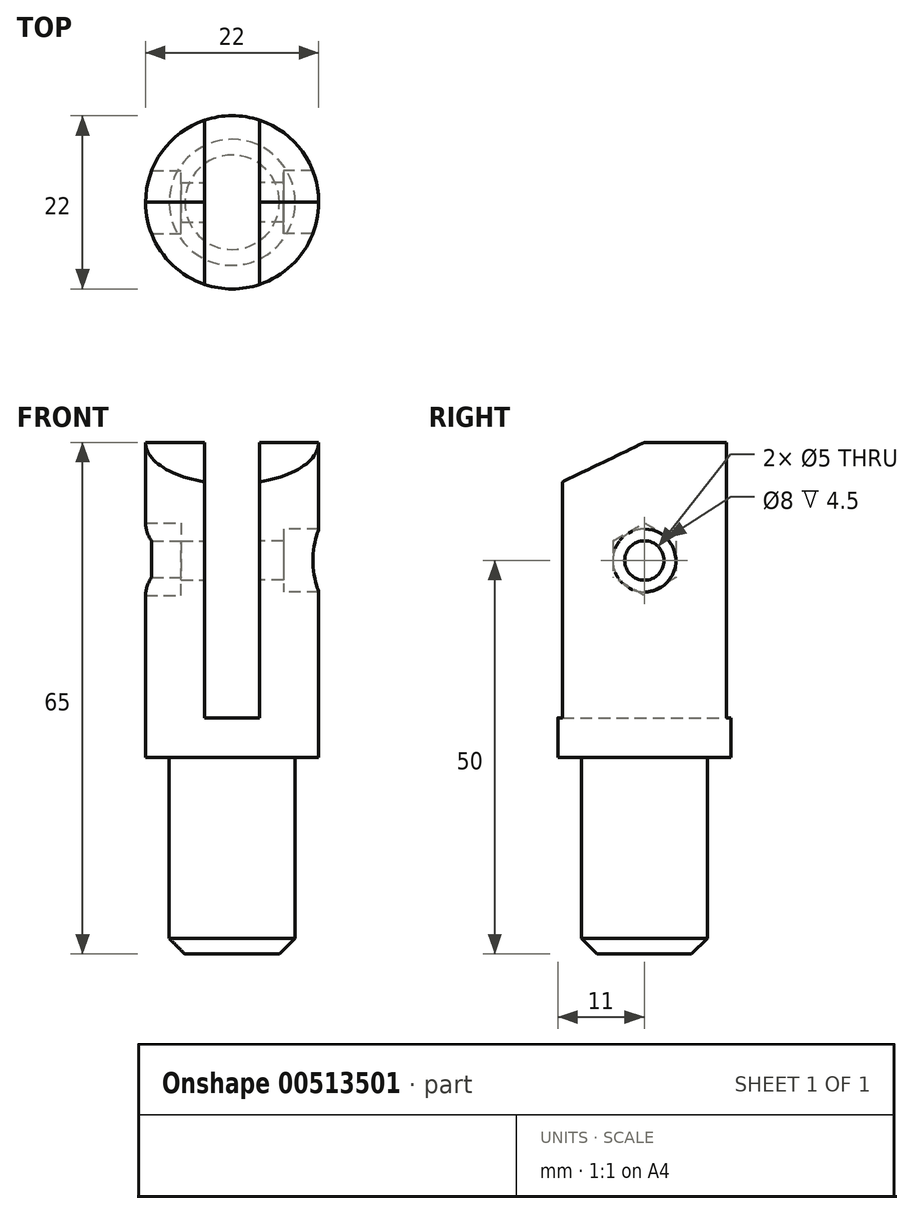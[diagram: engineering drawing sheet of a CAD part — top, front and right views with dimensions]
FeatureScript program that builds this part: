
annotation { "Feature Type Name" : "Feature", "Feature Type Description" : "" }
export const myFeature = defineFeature(function(context is Context, id is Id, definition is map)
    precondition{}
    {
        {
            var Q0;
            Q0=qCreatedBy(makeId("Top.planeOp"),FACE);
            var sketch = newSketch(context, id + "F0", { "sketchPlane" : qUnion([Q0])});
            skCircle(sketch, "E0", {"center": v(0, 0) * mm, "radius": 11 * mm});
            skSolve(sketch);
        }
        {
            var Q0;
            Q0=makeQuery(id+"F0.imprint","IMPRINT",FACE,{"disambiguationData":[TD([[makeQuery(id+"F0.imprint","IMPRINT",EDGE,{"derivedFrom":sQuery(id+"F0.wireOp",EDGE,"E0")}),1.0]])]});
            extrude(context, id + "F1", {"entities" : qUnion([Q0]), "depth" : 40 * mm, "offsetDistance" : 25 * mm});
        }
        {
            var Q0;
            Q0=makeQuery(id+"F1.opExtrude","CAP_FACE",FACE,{"disambiguationData":[OSD([sQuery(id+"F0.wireOp",EDGE,"E0")])],"isStart":false});
            var sketch = newSketch(context, id + "F2", { "sketchPlane" : qUnion([Q0])});
            skLineSegment(sketch, "E1.bottom", {"start": v(3.5, -20) * mm, "end": v(-3.5, -20) * mm});
            skLineSegment(sketch, "E1.top", {"start": v(3.5, 20) * mm, "end": v(-3.5, 20) * mm});
            skLineSegment(sketch, "E1.left", {"start": v(3.5, -20) * mm, "end": v(3.5, 20) * mm});
            skLineSegment(sketch, "E1.right", {"start": v(-3.5, -20) * mm, "end": v(-3.5, 20) * mm});
            skPoint(sketch, "E1.middle", {"position": v(0, 0) * mm});
            skSolve(sketch);
        }
        {
            var Q0;
            {var subQ0=sQuery(id+"F2.wireOp",EDGE,"E1.left");var subQ1=makeQuery(id+"F1.opExtrude","CAP_EDGE",EDGE,{"disambiguationData":[OSD([sQuery(id+"F0.wireOp",EDGE,"E0")])],"isStart":false});var subQ2=makeQuery(id+"F2.imprint","INTERSECT",VERTEX,{"disambiguationData":[OD(0.0)],"derivedFrom":[subQ1,subQ0]});Q0=makeQuery(id+"F2.imprint","IMPRINT",FACE,{"disambiguationData":[TD([[makeQuery(id+"F2.imprint","IMPRINT",EDGE,{"disambiguationData":[TD([[subQ2,-1.0]])],"derivedFrom":subQ0}),1.0]])]});}
            extrude(context, id + "F3", {"entities" : qUnion([Q0]), "operationType" : NewBodyOperationType.REMOVE, "oppositeDirection" : true, "depth" : 35 * mm, "offsetDistance" : 25 * mm});
        }
        {
            var Q0;
            Q0=makeQuery(id+"F3.boolean.opBoolean","COPY",FACE,{"derivedFrom":makeQuery(id+"F3.opExtrude","SWEPT_FACE",FACE,{"disambiguationData":[OSD([sQuery(id+"F2.wireOp",EDGE,"E1.right")])]})});
            var sketch = newSketch(context, id + "F4", { "sketchPlane" : qUnion([Q0])});
            skLineSegment(sketch, "E2", {"start": v(0, 40) * mm, "end": v(-10.43, 35) * mm});
            skSolve(sketch);
        }
        {
            var Q0;
            Q0=makeQuery(id+"F1.opExtrude","CAP_FACE",FACE,{"disambiguationData":[OSD([sQuery(id+"F0.wireOp",EDGE,"E0")])],"isStart":true});
            var sketch = newSketch(context, id + "F5", { "sketchPlane" : qUnion([Q0])});
            skCircle(sketch, "E3", {"center": v(0, 0) * mm, "radius": 8 * mm});
            skSolve(sketch);
        }
        {
            var Q0;
            {var subQ0=sQuery(id+"F4.wireOp",EDGE,"E2");Q0=makeQuery(id+"F4.imprint","IMPRINT",FACE,{"disambiguationData":[TD([[makeQuery(id+"F4.imprint","IMPRINT",EDGE,{"derivedFrom":subQ0}),-1.0]])]});}
            extrude(context, id + "F6", {"entities" : qUnion([Q0]), "operationType" : NewBodyOperationType.REMOVE, "endBound" : BoundingType.THROUGH_ALL, "oppositeDirection" : true, "depth" : 25 * mm, "offsetDistance" : 25 * mm});
        }
        {
            var Q0;
            Q0=makeQuery(id+"F3.boolean.opBoolean","COPY",FACE,{"derivedFrom":makeQuery(id+"F3.opExtrude","SWEPT_FACE",FACE,{"disambiguationData":[OSD([sQuery(id+"F2.wireOp",EDGE,"E1.left")])]})});
            var sketch = newSketch(context, id + "F7", { "sketchPlane" : qUnion([Q0])});
            skLineSegment(sketch, "E4", {"start": v(0, 40) * mm, "end": v(10.43, 35) * mm});
            skSolve(sketch);
        }
        {
            var Q0;
            {var subQ0=sQuery(id+"F7.wireOp",EDGE,"E4");Q0=makeQuery(id+"F7.imprint","IMPRINT",FACE,{"disambiguationData":[TD([[makeQuery(id+"F7.imprint","IMPRINT",EDGE,{"derivedFrom":subQ0}),1.0]])]});}
            extrude(context, id + "F8", {"entities" : qUnion([Q0]), "operationType" : NewBodyOperationType.REMOVE, "endBound" : BoundingType.THROUGH_ALL, "oppositeDirection" : true, "depth" : 25 * mm, "offsetDistance" : 25 * mm});
        }
        {
            var Q0;
            Q0=makeQuery(id+"F5.imprint","IMPRINT",FACE,{"disambiguationData":[TD([[makeQuery(id+"F5.imprint","IMPRINT",EDGE,{"derivedFrom":sQuery(id+"F5.wireOp",EDGE,"E3")}),1.0]])]});
            extrude(context, id + "F9", {"entities" : qUnion([Q0]), "operationType" : NewBodyOperationType.ADD, "depth" : 25 * mm, "offsetDistance" : 25 * mm});
        }
        {
            var Q0;
            Q0=makeQuery(id+"F3.boolean.opBoolean","COPY",FACE,{"derivedFrom":makeQuery(id+"F3.opExtrude","SWEPT_FACE",FACE,{"disambiguationData":[OSD([sQuery(id+"F2.wireOp",EDGE,"E1.left")])]})});
            var sketch = newSketch(context, id + "F10", { "sketchPlane" : qUnion([Q0])});
            skCircle(sketch, "E5", {"center": v(0, 25) * mm, "radius": 2.5 * mm});
            skSolve(sketch);
        }
        {
            var Q0;
            Q0 = qSketchRegion(id + "F10", true);
            extrude(context, id + "F11", {"entities" : qUnion([Q0]), "operationType" : NewBodyOperationType.REMOVE, "endBound" : BoundingType.THROUGH_ALL, "oppositeDirection" : true, "depth" : 25 * mm, "offsetDistance" : 25 * mm});
        }
        {
            var Q0;
            Q0=makeQuery(id+"F3.boolean.opBoolean","COPY",FACE,{"derivedFrom":makeQuery(id+"F3.opExtrude","SWEPT_FACE",FACE,{"disambiguationData":[OSD([sQuery(id+"F2.wireOp",EDGE,"E1.right")])]})});
            var sketch = newSketch(context, id + "F12", { "sketchPlane" : qUnion([Q0])});
            skCircle(sketch, "E6", {"center": v(0, 25) * mm, "radius": 2.5 * mm});
            skSolve(sketch);
        }
        {
            var Q0;
            Q0 = qSketchRegion(id + "F12", true);
            extrude(context, id + "F13", {"entities" : qUnion([Q0]), "operationType" : NewBodyOperationType.REMOVE, "endBound" : BoundingType.THROUGH_ALL, "oppositeDirection" : true, "depth" : 25 * mm, "offsetDistance" : 25 * mm});
        }
        {
            var Q0;
            Q0=makeQuery(id+"F9.opExtrude","CAP_FACE",FACE,{"disambiguationData":[OSD([sQuery(id+"F5.wireOp",EDGE,"E3")])],"isStart":false});
            chamfer(context, id + "F14", {"entities" : qUnion([Q0]), "width" : 2 * mm, "tangentPropagation" : true});
        }
        {
            var Q0;
            Q0=makeQuery(id+"F3.boolean.opBoolean","COPY",FACE,{"derivedFrom":makeQuery(id+"F3.opExtrude","SWEPT_FACE",FACE,{"disambiguationData":[OSD([sQuery(id+"F2.wireOp",EDGE,"E1.right")])]})});
            cPlane(context, id + "F15", {"entities" : qUnion([Q0]), "cplaneType" : CPlaneType.OFFSET, "offset" : 3 * mm, "oppositeDirection" : true, "width" : 150 * mm, "height" : 150 * mm});
        }
        {
            var Q0;
            Q0=qCreatedBy(id+"F15.planeOp",FACE);
            var sketch = newSketch(context, id + "F16", { "sketchPlane" : qUnion([Q0])});
            skCircle(sketch, "E7", {"center": v(0, 25.17) * mm, "radius": 4 * mm});
            skCircle(sketch, "E8.cCircle", {"center": v(0, 25.17) * mm, "radius": 4 * mm, "construction": true});
            skLineSegment(sketch, "E8.0", {"start": v(4, 27.47) * mm, "end": v(4, 22.86) * mm});
            skLineSegment(sketch, "E8.1", {"start": v(4, 22.86) * mm, "end": v(0, 20.55) * mm});
            skLineSegment(sketch, "E8.2", {"start": v(0, 20.55) * mm, "end": v(-4, 22.86) * mm});
            skLineSegment(sketch, "E8.3", {"start": v(-4, 22.86) * mm, "end": v(-4, 27.47) * mm});
            skLineSegment(sketch, "E8.4", {"start": v(-4, 27.47) * mm, "end": v(0, 29.78) * mm});
            skLineSegment(sketch, "E8.5", {"start": v(0, 29.78) * mm, "end": v(4, 27.47) * mm});
            skPoint(sketch, "E8.0.midPoint", {"position": v(4, 25.17) * mm});
            skSolve(sketch);
        }
        {
            var Q0;
            Q0 = qSketchRegion(id + "F16", true);
            extrude(context, id + "F17", {"entities" : qUnion([Q0]), "operationType" : NewBodyOperationType.REMOVE, "endBound" : BoundingType.THROUGH_ALL, "oppositeDirection" : true, "depth" : 25 * mm, "offsetDistance" : 25 * mm});
        }
        {
            var Q0;
            Q0=makeQuery(id+"F3.boolean.opBoolean","COPY",FACE,{"derivedFrom":makeQuery(id+"F3.opExtrude","SWEPT_FACE",FACE,{"disambiguationData":[OSD([sQuery(id+"F2.wireOp",EDGE,"E1.left")])]})});
            cPlane(context, id + "F18", {"entities" : qUnion([Q0]), "cplaneType" : CPlaneType.OFFSET, "offset" : 3 * mm, "oppositeDirection" : true, "width" : 150 * mm, "height" : 150 * mm});
        }
        {
            var Q0;
            Q0=qCreatedBy(id+"F18.planeOp",FACE);
            var sketch = newSketch(context, id + "F19", { "sketchPlane" : qUnion([Q0])});
            skCircle(sketch, "E9", {"center": v(0, 25) * mm, "radius": 4 * mm});
            skSolve(sketch);
        }
        {
            var Q0;
            Q0 = qSketchRegion(id + "F19", true);
            extrude(context, id + "F20", {"entities" : qUnion([Q0]), "operationType" : NewBodyOperationType.REMOVE, "endBound" : BoundingType.THROUGH_ALL, "oppositeDirection" : true, "depth" : 25 * mm, "offsetDistance" : 25 * mm});
        }
    });
